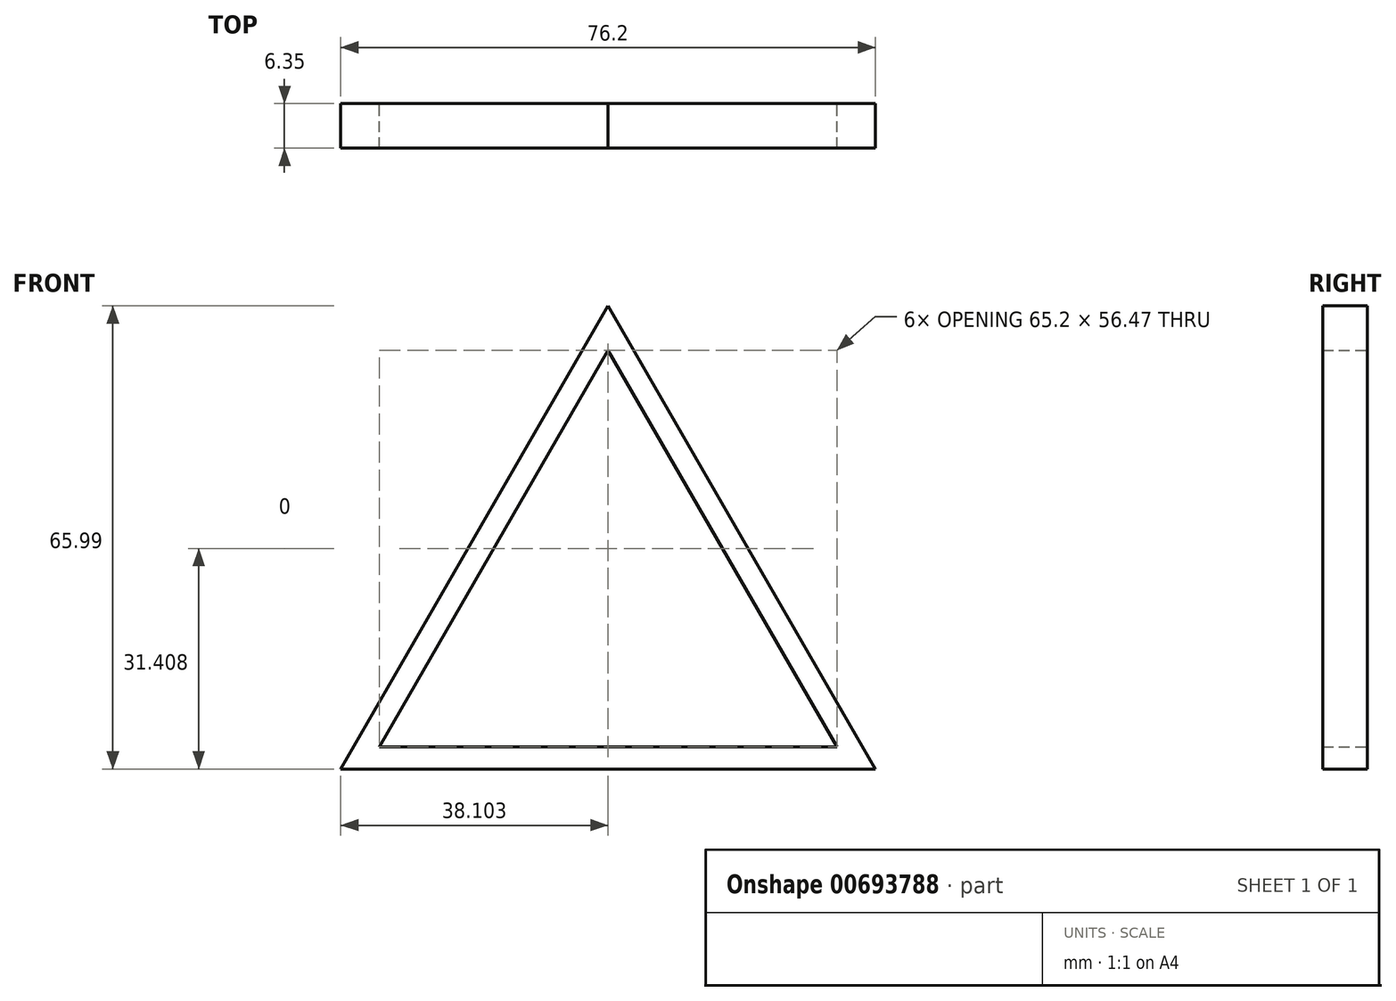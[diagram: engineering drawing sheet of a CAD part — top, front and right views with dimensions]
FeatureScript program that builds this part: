
annotation { "Feature Type Name" : "Feature", "Feature Type Description" : "" }
export const myFeature = defineFeature(function(context is Context, id is Id, definition is map)
    precondition{}
    {
        {
            var Q0;
            Q0=qCreatedBy(makeId("Front.planeOp"),FACE);
            var sketch = newSketch(context, id + "F0", { "sketchPlane" : qUnion([Q0])});
            skLineSegment(sketch, "E0", {"start": v(-26.29, 0) * mm, "end": v(49.91, 0) * mm});
            skLineSegment(sketch, "E1", {"start": v(49.91, 0) * mm, "end": v(11.81, 66) * mm});
            skLineSegment(sketch, "E2", {"start": v(11.81, 66) * mm, "end": v(-26.29, 0) * mm});
            skPoint(sketch, "E3", {"position": v(-20.79, 3.17) * mm});
            skPoint(sketch, "E4", {"position": v(11.81, 59.64) * mm});
            skPoint(sketch, "E5", {"position": v(44.41, 3.18) * mm});
            skLineSegment(sketch, "E6", {"start": v(-20.79, 3.18) * mm, "end": v(11.81, 59.64) * mm});
            skLineSegment(sketch, "E7", {"start": v(11.81, 59.64) * mm, "end": v(44.41, 3.18) * mm});
            skLineSegment(sketch, "E8", {"start": v(-20.79, 3.18) * mm, "end": v(44.41, 3.18) * mm});
            skSolve(sketch);
        }
        {
            var Q0;
            Q0=makeQuery(id+"F0.imprint","IMPRINT",FACE,{"disambiguationData":[TD([[makeQuery(id+"F0.imprint","IMPRINT",EDGE,{"derivedFrom":sQuery(id+"F0.wireOp",EDGE,"E0")}),1.0]])]});
            extrude(context, id + "F1", {"entities" : qUnion([Q0]), "depth" : 6.35 * mm, "offsetDistance" : 25.4 * mm});
        }
    });
